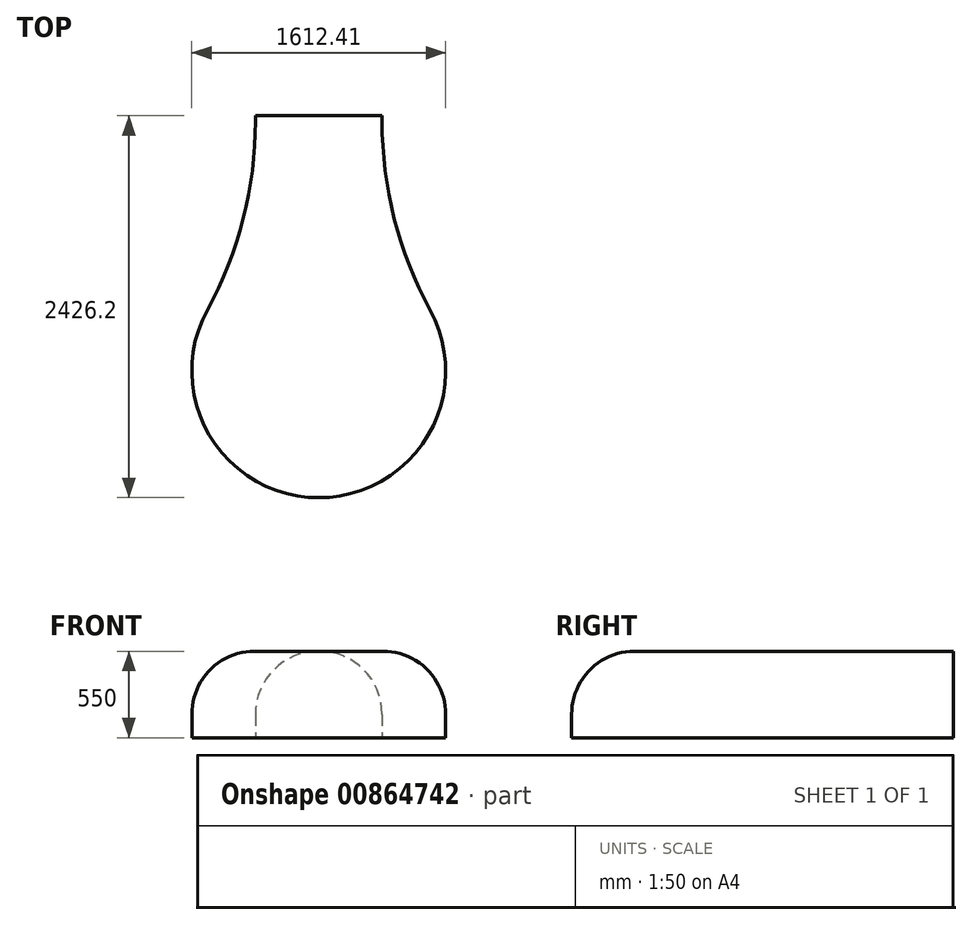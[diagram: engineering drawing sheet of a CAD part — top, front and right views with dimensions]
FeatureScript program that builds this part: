
annotation { "Feature Type Name" : "Feature", "Feature Type Description" : "" }
export const myFeature = defineFeature(function(context is Context, id is Id, definition is map)
    precondition{}
    {
        {
            var Q0;
            Q0=qCreatedBy(makeId("Top.planeOp"),FACE);
            var sketch = newSketch(context, id + "F0", { "sketchPlane" : qUnion([Q0])});
            skLineSegment(sketch, "E0.bottom", {"start": v(0, 0) * mm, "end": v(804.13, 0) * mm});
            skLineSegment(sketch, "E0.top", {"start": v(0, 1620) * mm, "end": v(804.13, 1620) * mm});
            skLineSegment(sketch, "E0.left", {"start": v(0, 0) * mm, "end": v(0, 1620) * mm});
            skLineSegment(sketch, "E0.right", {"start": v(804.13, 0) * mm, "end": v(804.13, 1620) * mm});
            skCircle(sketch, "E1", {"center": v(402.07, 0) * mm, "radius": 806.2 * mm});
            skSolve(sketch);
        }
        {
            var Q0;
            {var subQ0=sQuery(id+"F0.wireOp",EDGE,"E0.top");Q0=makeQuery(id+"F0.imprint","IMPRINT",FACE,{"disambiguationData":[TD([[makeQuery(id+"F0.imprint","IMPRINT",EDGE,{"derivedFrom":subQ0}),-1.0]])]});}
            var Q1;
            {var subQ0=sQuery(id+"F0.wireOp",EDGE,"E0.bottom");Q1=makeQuery(id+"F0.imprint","IMPRINT",FACE,{"disambiguationData":[TD([[makeQuery(id+"F0.imprint","IMPRINT",EDGE,{"derivedFrom":subQ0}),1.0]])]});}
            var Q2;
            {var subQ0=sQuery(id+"F0.wireOp",EDGE,"E0.bottom");Q2=makeQuery(id+"F0.imprint","IMPRINT",FACE,{"disambiguationData":[TD([[makeQuery(id+"F0.imprint","IMPRINT",EDGE,{"derivedFrom":subQ0}),-1.0]])]});}
            extrude(context, id + "F1", {"entities" : qUnion([Q0, Q1, Q2]), "depth" : 550 * mm, "offsetDistance" : 25 * mm});
        }
        {
            var Q0;
            Q0=makeQuery(id+"F1.opExtrude","SWEPT_EDGE",EDGE,{"disambiguationData":[OSD([sQuery(id+"F0.wireOp",EDGE,"E0.left"),sQuery(id+"F0.wireOp",EDGE,"E1")])]});
            var Q1;
            Q1=makeQuery(id+"F1.opExtrude","SWEPT_EDGE",EDGE,{"disambiguationData":[OSD([sQuery(id+"F0.wireOp",EDGE,"E0.right"),sQuery(id+"F0.wireOp",EDGE,"E1")])]});
            fillet(context, id + "F2", {"entities" : qUnion([Q0, Q1]), "radius" : 2500 * mm, "tangentPropagation" : true, "allowEdgeOverflow" : false});
        }
        {
            var Q0;
            {var subQ0=sQuery(id+"F0.wireOp",EDGE,"E1");var subQ1=sQuery(id+"F0.wireOp",EDGE,"E0.right");Q0=makeQuery(id+"F2.opFillet","BLEND_EDGE",EDGE,{"blendedFrom":[makeQuery(id+"F1.opExtrude","SWEPT_EDGE",EDGE,{"disambiguationData":[OSD([subQ1,subQ0])]}),makeQuery(id+"F1.opExtrude","CAP_FACE",FACE,{"disambiguationData":[OSD([sQuery(id+"F0.wireOp",EDGE,"E0.top"),sQuery(id+"F0.wireOp",EDGE,"E0.left"),subQ1,subQ0])],"isStart":false})],"blendedInto":[makeQuery(id+"F1.opExtrude","CAP_FACE",FACE,{"disambiguationData":[OSD([sQuery(id+"F0.wireOp",EDGE,"E0.top"),sQuery(id+"F0.wireOp",EDGE,"E0.left"),subQ1,subQ0])],"isStart":false})]});}
            var Q1;
            Q1=makeQuery(id+"F1.opExtrude","CAP_EDGE",EDGE,{"disambiguationData":[OSD([sQuery(id+"F0.wireOp",EDGE,"E1")])],"isStart":false});
            var Q2;
            {var subQ0=sQuery(id+"F0.wireOp",EDGE,"E1");var subQ1=sQuery(id+"F0.wireOp",EDGE,"E0.left");Q2=makeQuery(id+"F2.opFillet","BLEND_EDGE",EDGE,{"blendedFrom":[makeQuery(id+"F1.opExtrude","SWEPT_EDGE",EDGE,{"disambiguationData":[OSD([subQ1,subQ0])]}),makeQuery(id+"F1.opExtrude","CAP_FACE",FACE,{"disambiguationData":[OSD([sQuery(id+"F0.wireOp",EDGE,"E0.top"),subQ1,sQuery(id+"F0.wireOp",EDGE,"E0.right"),subQ0])],"isStart":false})],"blendedInto":[makeQuery(id+"F1.opExtrude","CAP_FACE",FACE,{"disambiguationData":[OSD([sQuery(id+"F0.wireOp",EDGE,"E0.top"),subQ1,sQuery(id+"F0.wireOp",EDGE,"E0.right"),subQ0])],"isStart":false})]});}
            fillet(context, id + "F3", {"entities" : qUnion([Q0, Q1, Q2]), "radius" : 400 * mm, "tangentPropagation" : true, "allowEdgeOverflow" : false});
        }
    });
